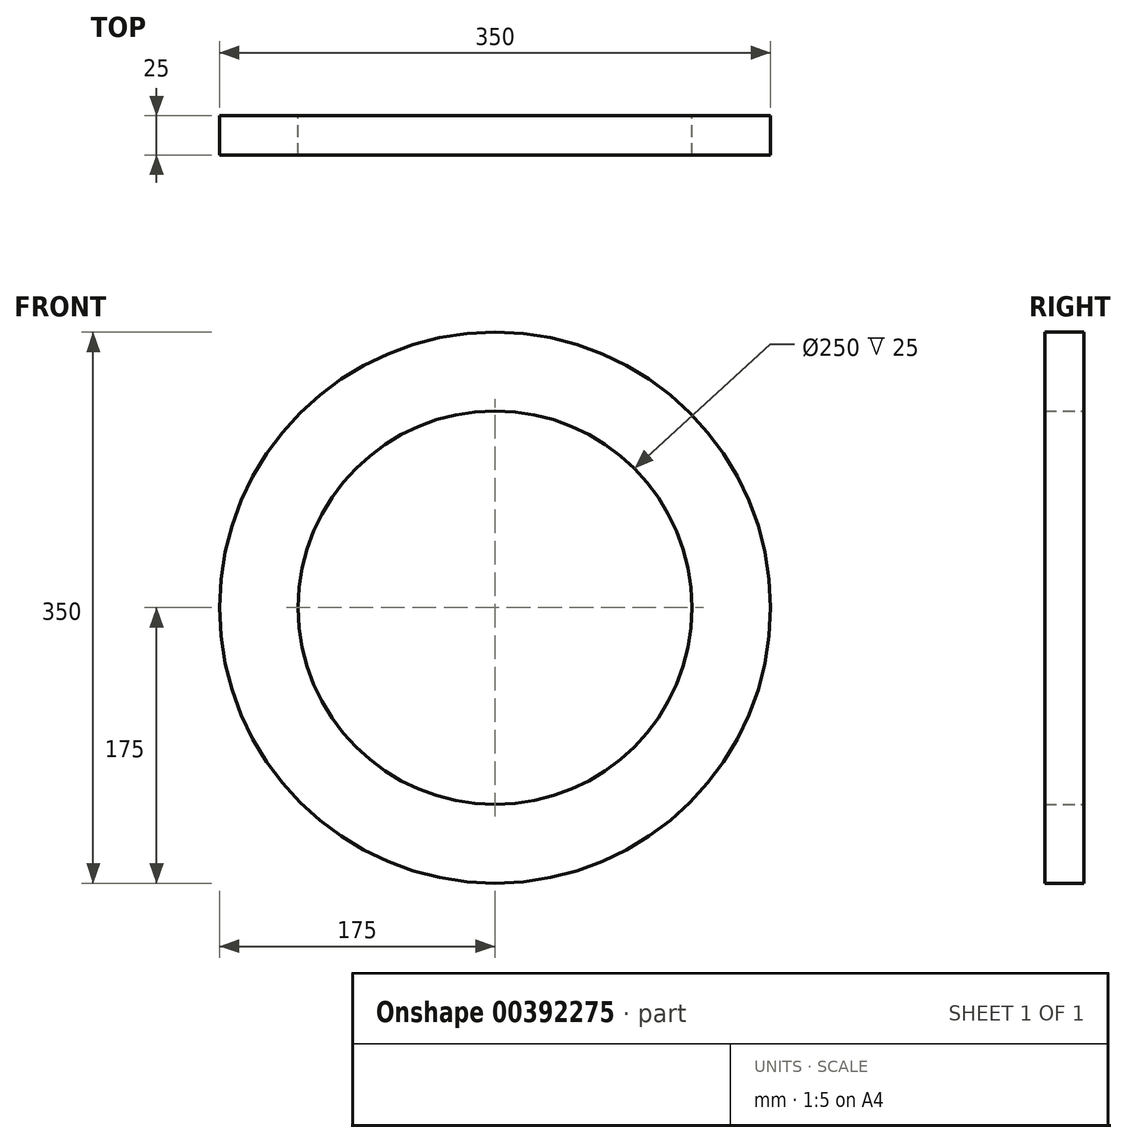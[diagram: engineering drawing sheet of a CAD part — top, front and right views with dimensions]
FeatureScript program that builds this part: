
annotation { "Feature Type Name" : "Feature", "Feature Type Description" : "" }
export const myFeature = defineFeature(function(context is Context, id is Id, definition is map)
    precondition{}
    {
        {
            var Q0;
            Q0=qCreatedBy(makeId("Front.planeOp"),FACE);
            var sketch = newSketch(context, id + "F0", { "sketchPlane" : qUnion([Q0])});
            skCircle(sketch, "E0", {"center": v(0, 0) * mm, "radius": 175 * mm});
            skCircle(sketch, "E1", {"center": v(0, 0) * mm, "radius": 125 * mm});
            skSolve(sketch);
        }
        {
            var Q0;
            Q0=makeQuery(id+"F0.imprint","IMPRINT",FACE,{"disambiguationData":[TD([[makeQuery(id+"F0.imprint","IMPRINT",EDGE,{"derivedFrom":sQuery(id+"F0.wireOp",EDGE,"E0")}),1.0]])]});
            extrude(context, id + "F1", {"entities" : qUnion([Q0]), "depth" : 25 * mm});
        }
    });
